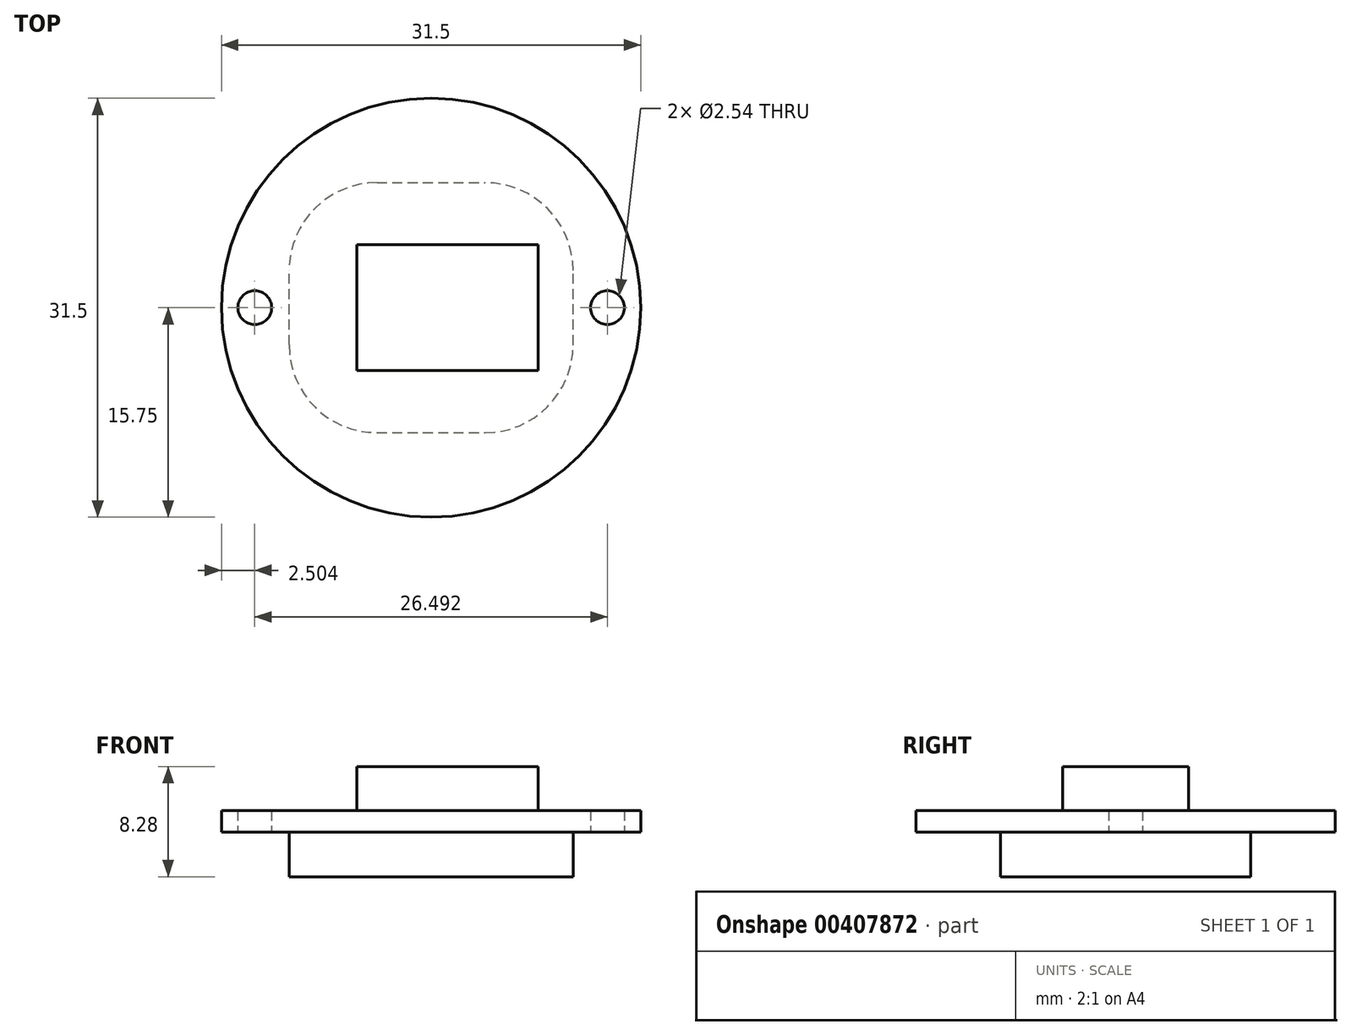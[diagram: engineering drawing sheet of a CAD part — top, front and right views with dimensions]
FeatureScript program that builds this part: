
annotation { "Feature Type Name" : "Feature", "Feature Type Description" : "" }
export const myFeature = defineFeature(function(context is Context, id is Id, definition is map)
    precondition{}
    {
        {
            var Q0;
            Q0=qCreatedBy(makeId("Top.planeOp"),FACE);
            var sketch = newSketch(context, id + "F0", { "sketchPlane" : qUnion([Q0])});
            skCircle(sketch, "E0", {"center": v(0, 0) * mm, "radius": 15.75 * mm});
            skCircle(sketch, "E1", {"center": v(13.25, 0) * mm, "radius": 1.27 * mm});
            skCircle(sketch, "E2", {"center": v(-13.25, 0) * mm, "radius": 1.27 * mm});
            skSolve(sketch);
        }
        {
            var Q0;
            Q0 = qSketchRegion(id + "F0", true);
            extrude(context, id + "F1", {"entities" : qUnion([Q0]), "depth" : 1.63 * mm});
        }
        {
            var Q0;
            Q0=makeQuery(id+"F1.opExtrude","CAP_FACE",FACE,{"disambiguationData":[OSD([sQuery(id+"F0.wireOp",EDGE,"E0"),sQuery(id+"F0.wireOp",EDGE,"E1"),sQuery(id+"F0.wireOp",EDGE,"E2")])],"isStart":false});
            var sketch = newSketch(context, id + "F2", { "sketchPlane" : qUnion([Q0])});
            skLineSegment(sketch, "E3", {"start": v(8.05, 4.74) * mm, "end": v(8.05, -4.73) * mm});
            skLineSegment(sketch, "E4", {"start": v(-5.59, 4.74) * mm, "end": v(-5.59, -4.73) * mm});
            skLineSegment(sketch, "E5", {"start": v(-5.59, 4.74) * mm, "end": v(8.05, 4.74) * mm});
            skLineSegment(sketch, "E6", {"start": v(-5.59, -4.73) * mm, "end": v(8.05, -4.73) * mm});
            skSolve(sketch);
        }
        {
            var Q0;
            Q0 = qSketchRegion(id + "F2", true);
            extrude(context, id + "F3", {"entities" : qUnion([Q0]), "operationType" : NewBodyOperationType.ADD, "depth" : 3.3 * mm});
        }
        {
            var Q0;
            Q0=qCreatedBy(makeId("Top.planeOp"),FACE);
            var sketch = newSketch(context, id + "F4", { "sketchPlane" : qUnion([Q0])});
            skLineSegment(sketch, "E7", {"start": v(10.67, -9.4) * mm, "end": v(10.67, 9.4) * mm});
            skLineSegment(sketch, "E8", {"start": v(-10.67, -9.4) * mm, "end": v(-10.67, 9.4) * mm});
            skLineSegment(sketch, "E9", {"start": v(-10.67, 9.4) * mm, "end": v(10.67, 9.4) * mm});
            skLineSegment(sketch, "E10", {"start": v(-10.67, -9.4) * mm, "end": v(10.67, -9.4) * mm});
            skSolve(sketch);
        }
        {
            var Q0;
            Q0 = qSketchRegion(id + "F4", true);
            extrude(context, id + "F5", {"entities" : qUnion([Q0]), "operationType" : NewBodyOperationType.ADD, "oppositeDirection" : true, "depth" : 3.35 * mm});
        }
        {
            var Q0;
            Q0=makeQuery(id+"F5.opExtrude","SWEPT_EDGE",EDGE,{"disambiguationData":[OSD([sQuery(id+"F4.wireOp",EDGE,"E7"),sQuery(id+"F4.wireOp",EDGE,"E10")])]});
            var Q1;
            Q1=makeQuery(id+"F5.opExtrude","SWEPT_EDGE",EDGE,{"disambiguationData":[OSD([sQuery(id+"F4.wireOp",EDGE,"E8"),sQuery(id+"F4.wireOp",EDGE,"E10")])]});
            var Q2;
            Q2=makeQuery(id+"F5.opExtrude","SWEPT_EDGE",EDGE,{"disambiguationData":[OSD([sQuery(id+"F4.wireOp",EDGE,"E8"),sQuery(id+"F4.wireOp",EDGE,"E9")])]});
            var Q3;
            Q3=makeQuery(id+"F5.opExtrude","SWEPT_EDGE",EDGE,{"disambiguationData":[OSD([sQuery(id+"F4.wireOp",EDGE,"E7"),sQuery(id+"F4.wireOp",EDGE,"E9")])]});
            fillet(context, id + "F6", {"entities" : qUnion([Q0, Q1, Q2, Q3]), "radius" : 6.6 * mm, "tangentPropagation" : true, "allowEdgeOverflow" : false});
        }
    });
